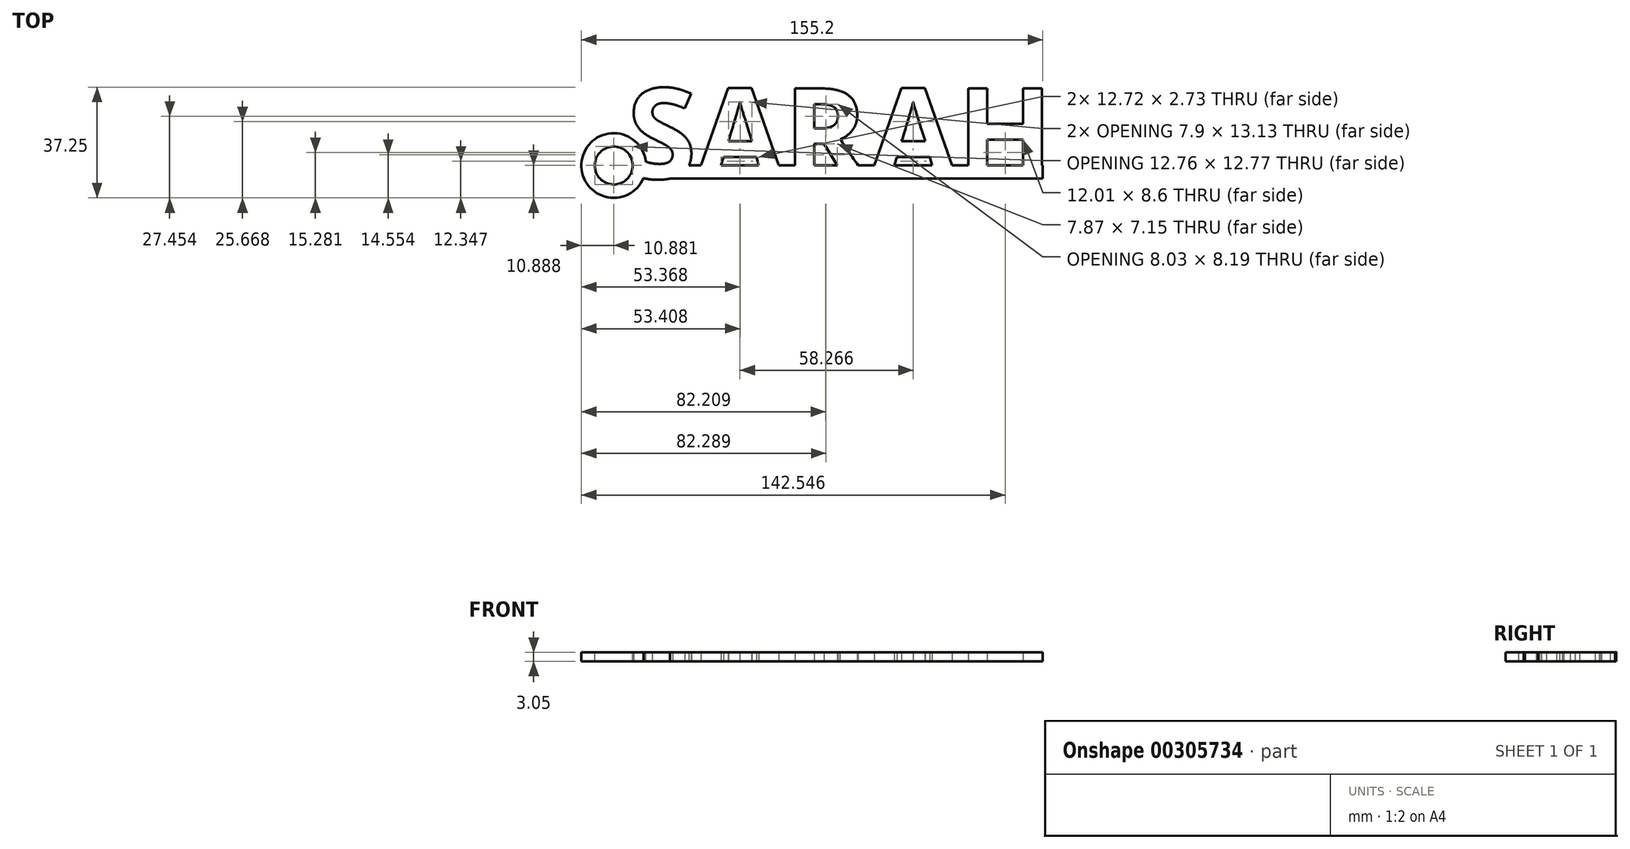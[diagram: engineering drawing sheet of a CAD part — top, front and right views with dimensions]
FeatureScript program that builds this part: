
annotation { "Feature Type Name" : "Feature", "Feature Type Description" : "" }
export const myFeature = defineFeature(function(context is Context, id is Id, definition is map)
    precondition{}
    {
        {
            var Q0;
            Q0=qCreatedBy(makeId("Top.planeOp"),FACE);
            var sketch = newSketch(context, id + "F0", { "sketchPlane" : qUnion([Q0])});
            skText(sketch, "E0", { "text": "SARAH\n", "fontName": "OpenSans-Bold.ttf"});
            skLineSegment(sketch, "E1.bottom", {"start": v(-99.27, -15.53) * mm, "end": v(31.63, -15.53) * mm});
            skLineSegment(sketch, "E1.top", {"start": v(-87.75, -11.04) * mm, "end": v(31.63, -11.04) * mm});
            skLineSegment(sketch, "E1.left", {"start": v(-108.26, -15.73) * mm, "end": v(-108.26, -11.43) * mm});
            skLineSegment(sketch, "E1.right", {"start": v(31.63, -15.53) * mm, "end": v(31.63, -11.04) * mm});
            const initialGuessF0  = {"E0": [-0.10826, -0.01553, 1, 0, 0.03059]};
            skSetInitialGuess(sketch, initialGuessF0);
            skSolve(sketch);
        }
        {
            var Q0;
            {var subQ0=sQuery(id+"F0.wireOp",EDGE,"E0.sketch_text.stroke-2");Q0=makeQuery(id+"F0.imprint","IMPRINT",FACE,{"disambiguationData":[TD([[makeQuery(id+"F0.imprint","IMPRINT",EDGE,{"derivedFrom":subQ0}),-1.0]])]});}
            var Q1;
            {var subQ3=sQuery(id+"F0.wireOp",EDGE,"E0.sketch_text.stroke-1");var subQ7=sQuery(id+"F0.wireOp",EDGE,"E0.sketch_text.stroke-0");var subQ8=makeQuery(id+"F0.imprint","INTERSECT",VERTEX,{"derivedFrom":[subQ7,subQ3]});Q1=makeQuery(id+"F0.imprint","IMPRINT",FACE,{"disambiguationData":[TD([[makeQuery(id+"F0.imprint","IMPRINT",EDGE,{"disambiguationData":[TD([[subQ8,1.0]])],"derivedFrom":subQ7}),1.0]])]});}
            var Q2;
            {var subQ0=sQuery(id+"F0.wireOp",EDGE,"E1.bottom");var subQ1=sQuery(id+"F0.wireOp",EDGE,"E0.sketch_text.stroke-30");var subQ2=makeQuery(id+"F0.imprint","INTERSECT",VERTEX,{"derivedFrom":[subQ1,subQ0]});Q2=makeQuery(id+"F0.imprint","IMPRINT",FACE,{"disambiguationData":[TD([[makeQuery(id+"F0.imprint","IMPRINT",EDGE,{"disambiguationData":[TD([[subQ2,1.0]])],"derivedFrom":subQ1}),-1.0]])]});}
            var Q3;
            {var subQ8=sQuery(id+"F0.wireOp",EDGE,"E0.sketch_text.stroke-29");Q3=makeQuery(id+"F0.imprint","IMPRINT",FACE,{"disambiguationData":[TD([[makeQuery(id+"F0.imprint","IMPRINT",EDGE,{"derivedFrom":subQ8}),-1.0]])]});}
            var Q4;
            {var subQ0=sQuery(id+"F0.wireOp",EDGE,"E1.bottom");var subQ1=sQuery(id+"F0.wireOp",EDGE,"E0.sketch_text.stroke-28");var subQ2=makeQuery(id+"F0.imprint","INTERSECT",VERTEX,{"derivedFrom":[subQ1,subQ0]});Q4=makeQuery(id+"F0.imprint","IMPRINT",FACE,{"disambiguationData":[TD([[makeQuery(id+"F0.imprint","IMPRINT",EDGE,{"disambiguationData":[TD([[subQ2,-1.0]])],"derivedFrom":subQ1}),-1.0]])]});}
            var Q5;
            {var subQ0=sQuery(id+"F0.wireOp",EDGE,"E1.bottom");var subQ1=sQuery(id+"F0.wireOp",EDGE,"E0.sketch_text.stroke-34");var subQ2=makeQuery(id+"F0.imprint","INTERSECT",VERTEX,{"derivedFrom":[subQ1,subQ0]});Q5=makeQuery(id+"F0.imprint","IMPRINT",FACE,{"disambiguationData":[TD([[makeQuery(id+"F0.imprint","IMPRINT",EDGE,{"disambiguationData":[TD([[subQ2,1.0]])],"derivedFrom":subQ1}),1.0]])]});}
            var Q6;
            {var subQ0=sQuery(id+"F0.wireOp",EDGE,"E1.bottom");var subQ1=sQuery(id+"F0.wireOp",EDGE,"E0.sketch_text.stroke-47");var subQ2=makeQuery(id+"F0.imprint","INTERSECT",VERTEX,{"derivedFrom":[subQ1,subQ0]});Q6=makeQuery(id+"F0.imprint","IMPRINT",FACE,{"disambiguationData":[TD([[makeQuery(id+"F0.imprint","IMPRINT",EDGE,{"disambiguationData":[TD([[subQ2,1.0]])],"derivedFrom":subQ1}),-1.0]])]});}
            var Q7;
            Q7=makeQuery(id+"F0.imprint","IMPRINT",FACE,{"disambiguationData":[TD([[makeQuery(id+"F0.imprint","IMPRINT",EDGE,{"derivedFrom":sQuery(id+"F0.wireOp",EDGE,"E0.sketch_text.stroke-40")}),-1.0]])]});
            var Q8;
            {var subQ0=sQuery(id+"F0.wireOp",EDGE,"E1.bottom");var subQ5=sQuery(id+"F0.wireOp",EDGE,"E0.sketch_text.stroke-57");var subQ7=makeQuery(id+"F0.imprint","INTERSECT",VERTEX,{"derivedFrom":[subQ5,subQ0]});Q8=makeQuery(id+"F0.imprint","IMPRINT",FACE,{"disambiguationData":[TD([[makeQuery(id+"F0.imprint","IMPRINT",EDGE,{"disambiguationData":[TD([[subQ7,-1.0]])],"derivedFrom":subQ5}),-1.0]])]});}
            var Q9;
            {var subQ0=sQuery(id+"F0.wireOp",EDGE,"E1.bottom");var subQ1=sQuery(id+"F0.wireOp",EDGE,"E0.sketch_text.stroke-61");var subQ2=makeQuery(id+"F0.imprint","INTERSECT",VERTEX,{"derivedFrom":[subQ1,subQ0]});Q9=makeQuery(id+"F0.imprint","IMPRINT",FACE,{"disambiguationData":[TD([[makeQuery(id+"F0.imprint","IMPRINT",EDGE,{"disambiguationData":[TD([[subQ2,1.0]])],"derivedFrom":subQ1}),-1.0]])]});}
            var Q10;
            {var subQ8=sQuery(id+"F0.wireOp",EDGE,"E0.sketch_text.stroke-60");Q10=makeQuery(id+"F0.imprint","IMPRINT",FACE,{"disambiguationData":[TD([[makeQuery(id+"F0.imprint","IMPRINT",EDGE,{"derivedFrom":subQ8}),-1.0]])]});}
            var Q11;
            {var subQ0=sQuery(id+"F0.wireOp",EDGE,"E1.bottom");var subQ1=sQuery(id+"F0.wireOp",EDGE,"E0.sketch_text.stroke-59");var subQ2=makeQuery(id+"F0.imprint","INTERSECT",VERTEX,{"derivedFrom":[subQ1,subQ0]});Q11=makeQuery(id+"F0.imprint","IMPRINT",FACE,{"disambiguationData":[TD([[makeQuery(id+"F0.imprint","IMPRINT",EDGE,{"disambiguationData":[TD([[subQ2,-1.0]])],"derivedFrom":subQ1}),-1.0]])]});}
            var Q12;
            {var subQ0=sQuery(id+"F0.wireOp",EDGE,"E1.bottom");var subQ1=sQuery(id+"F0.wireOp",EDGE,"E0.sketch_text.stroke-74");var subQ2=makeQuery(id+"F0.imprint","INTERSECT",VERTEX,{"derivedFrom":[subQ1,subQ0]});Q12=makeQuery(id+"F0.imprint","IMPRINT",FACE,{"disambiguationData":[TD([[makeQuery(id+"F0.imprint","IMPRINT",EDGE,{"disambiguationData":[TD([[subQ2,1.0]])],"derivedFrom":subQ1}),-1.0]])]});}
            var Q13;
            {var subQ5=sQuery(id+"F0.wireOp",EDGE,"E0.sketch_text.stroke-73");Q13=makeQuery(id+"F0.imprint","IMPRINT",FACE,{"disambiguationData":[TD([[makeQuery(id+"F0.imprint","IMPRINT",EDGE,{"derivedFrom":subQ5}),-1.0]])]});}
            var Q14;
            {var subQ0=sQuery(id+"F0.wireOp",EDGE,"E1.bottom");var subQ1=sQuery(id+"F0.wireOp",EDGE,"E0.sketch_text.stroke-72");var subQ2=makeQuery(id+"F0.imprint","INTERSECT",VERTEX,{"derivedFrom":[subQ1,subQ0]});Q14=makeQuery(id+"F0.imprint","IMPRINT",FACE,{"disambiguationData":[TD([[makeQuery(id+"F0.imprint","IMPRINT",EDGE,{"disambiguationData":[TD([[subQ2,-1.0]])],"derivedFrom":subQ1}),-1.0]])]});}
            var Q15;
            {var subQ0=sQuery(id+"F0.wireOp",EDGE,"E1.bottom");var subQ1=sQuery(id+"F0.wireOp",EDGE,"E0.sketch_text.stroke-65");var subQ2=makeQuery(id+"F0.imprint","INTERSECT",VERTEX,{"derivedFrom":[subQ1,subQ0]});Q15=makeQuery(id+"F0.imprint","IMPRINT",FACE,{"disambiguationData":[TD([[makeQuery(id+"F0.imprint","IMPRINT",EDGE,{"disambiguationData":[TD([[subQ2,1.0]])],"derivedFrom":subQ1}),1.0]])]});}
            var Q16;
            {var subQ1=sQuery(id+"F0.wireOp",EDGE,"E0.sketch_text.stroke-55");var subQ3=sQuery(id+"F0.wireOp",EDGE,"E1.top");var subQ4=makeQuery(id+"F0.imprint","INTERSECT",VERTEX,{"derivedFrom":[subQ1,subQ3]});Q16=makeQuery(id+"F0.imprint","IMPRINT",FACE,{"disambiguationData":[TD([[makeQuery(id+"F0.imprint","IMPRINT",EDGE,{"disambiguationData":[TD([[subQ4,-1.0]])],"derivedFrom":subQ3}),-1.0]])]});}
            extrude(context, id + "F1", {"entities" : qUnion([Q0, Q1, Q2, Q3, Q4, Q5, Q6, Q7, Q8, Q9, Q10, Q11, Q12, Q13, Q14, Q15, Q16]), "depth" : 3.05 * mm});
        }
        {
            var Q0;
            Q0=makeQuery(id+"F1.opExtrude","CAP_FACE",FACE,{"disambiguationData":[OSD([sQuery(id+"F0.wireOp",EDGE,"E0.sketch_text.stroke-0"),sQuery(id+"F0.wireOp",EDGE,"E0.sketch_text.stroke-1"),sQuery(id+"F0.wireOp",EDGE,"E0.sketch_text.stroke-2"),sQuery(id+"F0.wireOp",EDGE,"E0.sketch_text.stroke-3"),sQuery(id+"F0.wireOp",EDGE,"E0.sketch_text.stroke-4"),sQuery(id+"F0.wireOp",EDGE,"E0.sketch_text.stroke-5"),sQuery(id+"F0.wireOp",EDGE,"E0.sketch_text.stroke-6"),sQuery(id+"F0.wireOp",EDGE,"E0.sketch_text.stroke-7"),sQuery(id+"F0.wireOp",EDGE,"E0.sketch_text.stroke-8"),sQuery(id+"F0.wireOp",EDGE,"E0.sketch_text.stroke-9"),sQuery(id+"F0.wireOp",EDGE,"E0.sketch_text.stroke-10"),sQuery(id+"F0.wireOp",EDGE,"E0.sketch_text.stroke-11"),sQuery(id+"F0.wireOp",EDGE,"E0.sketch_text.stroke-12"),sQuery(id+"F0.wireOp",EDGE,"E0.sketch_text.stroke-13"),sQuery(id+"F0.wireOp",EDGE,"E0.sketch_text.stroke-14"),sQuery(id+"F0.wireOp",EDGE,"E0.sketch_text.stroke-15"),sQuery(id+"F0.wireOp",EDGE,"E0.sketch_text.stroke-16"),sQuery(id+"F0.wireOp",EDGE,"E0.sketch_text.stroke-17"),sQuery(id+"F0.wireOp",EDGE,"E0.sketch_text.stroke-18"),sQuery(id+"F0.wireOp",EDGE,"E0.sketch_text.stroke-19"),sQuery(id+"F0.wireOp",EDGE,"E0.sketch_text.stroke-20"),sQuery(id+"F0.wireOp",EDGE,"E0.sketch_text.stroke-21"),sQuery(id+"F0.wireOp",EDGE,"E0.sketch_text.stroke-22"),sQuery(id+"F0.wireOp",EDGE,"E0.sketch_text.stroke-23"),sQuery(id+"F0.wireOp",EDGE,"E0.sketch_text.stroke-24"),sQuery(id+"F0.wireOp",EDGE,"E0.sketch_text.stroke-25"),sQuery(id+"F0.wireOp",EDGE,"E0.sketch_text.stroke-26"),sQuery(id+"F0.wireOp",EDGE,"E0.sketch_text.stroke-27"),sQuery(id+"F0.wireOp",EDGE,"E0.sketch_text.stroke-28"),sQuery(id+"F0.wireOp",EDGE,"E0.sketch_text.stroke-29"),sQuery(id+"F0.wireOp",EDGE,"E0.sketch_text.stroke-30"),sQuery(id+"F0.wireOp",EDGE,"E0.sketch_text.stroke-32"),sQuery(id+"F0.wireOp",EDGE,"E0.sketch_text.stroke-33"),sQuery(id+"F0.wireOp",EDGE,"E0.sketch_text.stroke-34"),sQuery(id+"F0.wireOp",EDGE,"E0.sketch_text.stroke-36"),sQuery(id+"F0.wireOp",EDGE,"E0.sketch_text.stroke-37"),sQuery(id+"F0.wireOp",EDGE,"E0.sketch_text.stroke-38"),sQuery(id+"F0.wireOp",EDGE,"E0.sketch_text.stroke-39"),sQuery(id+"F0.wireOp",EDGE,"E0.sketch_text.stroke-40"),sQuery(id+"F0.wireOp",EDGE,"E0.sketch_text.stroke-41"),sQuery(id+"F0.wireOp",EDGE,"E0.sketch_text.stroke-42"),sQuery(id+"F0.wireOp",EDGE,"E0.sketch_text.stroke-43"),sQuery(id+"F0.wireOp",EDGE,"E0.sketch_text.stroke-44"),sQuery(id+"F0.wireOp",EDGE,"E0.sketch_text.stroke-45"),sQuery(id+"F0.wireOp",EDGE,"E0.sketch_text.stroke-46"),sQuery(id+"F0.wireOp",EDGE,"E0.sketch_text.stroke-47"),sQuery(id+"F0.wireOp",EDGE,"E0.sketch_text.stroke-49"),sQuery(id+"F0.wireOp",EDGE,"E0.sketch_text.stroke-50"),sQuery(id+"F0.wireOp",EDGE,"E0.sketch_text.stroke-51"),sQuery(id+"F0.wireOp",EDGE,"E0.sketch_text.stroke-52"),sQuery(id+"F0.wireOp",EDGE,"E0.sketch_text.stroke-53"),sQuery(id+"F0.wireOp",EDGE,"E0.sketch_text.stroke-54"),sQuery(id+"F0.wireOp",EDGE,"E0.sketch_text.stroke-55"),sQuery(id+"F0.wireOp",EDGE,"E0.sketch_text.stroke-57"),sQuery(id+"F0.wireOp",EDGE,"E0.sketch_text.stroke-58"),sQuery(id+"F0.wireOp",EDGE,"E0.sketch_text.stroke-59"),sQuery(id+"F0.wireOp",EDGE,"E0.sketch_text.stroke-60"),sQuery(id+"F0.wireOp",EDGE,"E0.sketch_text.stroke-61"),sQuery(id+"F0.wireOp",EDGE,"E0.sketch_text.stroke-63"),sQuery(id+"F0.wireOp",EDGE,"E0.sketch_text.stroke-64"),sQuery(id+"F0.wireOp",EDGE,"E0.sketch_text.stroke-65"),sQuery(id+"F0.wireOp",EDGE,"E0.sketch_text.stroke-67"),sQuery(id+"F0.wireOp",EDGE,"E0.sketch_text.stroke-68"),sQuery(id+"F0.wireOp",EDGE,"E0.sketch_text.stroke-69"),sQuery(id+"F0.wireOp",EDGE,"E0.sketch_text.stroke-70"),sQuery(id+"F0.wireOp",EDGE,"E0.sketch_text.stroke-72"),sQuery(id+"F0.wireOp",EDGE,"E0.sketch_text.stroke-73"),sQuery(id+"F0.wireOp",EDGE,"E0.sketch_text.stroke-74"),sQuery(id+"F0.wireOp",EDGE,"E0.sketch_text.stroke-76"),sQuery(id+"F0.wireOp",EDGE,"E0.sketch_text.stroke-77"),sQuery(id+"F0.wireOp",EDGE,"E0.sketch_text.stroke-78"),sQuery(id+"F0.wireOp",EDGE,"E0.sketch_text.stroke-79"),sQuery(id+"F0.wireOp",EDGE,"E0.sketch_text.stroke-80"),sQuery(id+"F0.wireOp",EDGE,"E0.sketch_text.stroke-81"),sQuery(id+"F0.wireOp",EDGE,"E0.sketch_text.stroke-82"),sQuery(id+"F0.wireOp",EDGE,"E1.bottom"),sQuery(id+"F0.wireOp",EDGE,"E1.top")])],"isStart":false});
            var sketch = newSketch(context, id + "F2", { "sketchPlane" : qUnion([Q0])});
            skCircle(sketch, "E2", {"center": v(-112.68, -11.13) * mm, "radius": 10.9 * mm});
            skCircle(sketch, "E3", {"center": v(-112.68, -11.13) * mm, "radius": 6.4 * mm});
            skPoint(sketch, "E4", {"position": v(-106.3, -11.13) * mm});
            skSolve(sketch);
        }
        {
            var Q0;
            {var subQ1=makeQuery(id+"F1.opExtrude","CAP_EDGE",EDGE,{"disambiguationData":[OSD([sQuery(id+"F0.wireOp",EDGE,"E0.sketch_text.stroke-2")])],"isStart":false});var subQ3=sQuery(id+"F2.wireOp",EDGE,"E2");var subQ4=makeQuery(id+"F2.imprint","INTERSECT",VERTEX,{"derivedFrom":[subQ1,subQ3]});Q0=makeQuery(id+"F2.imprint","IMPRINT",FACE,{"disambiguationData":[TD([[makeQuery(id+"F2.imprint","IMPRINT",EDGE,{"disambiguationData":[TD([[subQ4,1.0]])],"derivedFrom":subQ3}),1.0]])]});}
            extrude(context, id + "F3", {"entities" : qUnion([Q0]), "operationType" : NewBodyOperationType.ADD, "oppositeDirection" : true, "depth" : 3.05 * mm});
        }
    });
